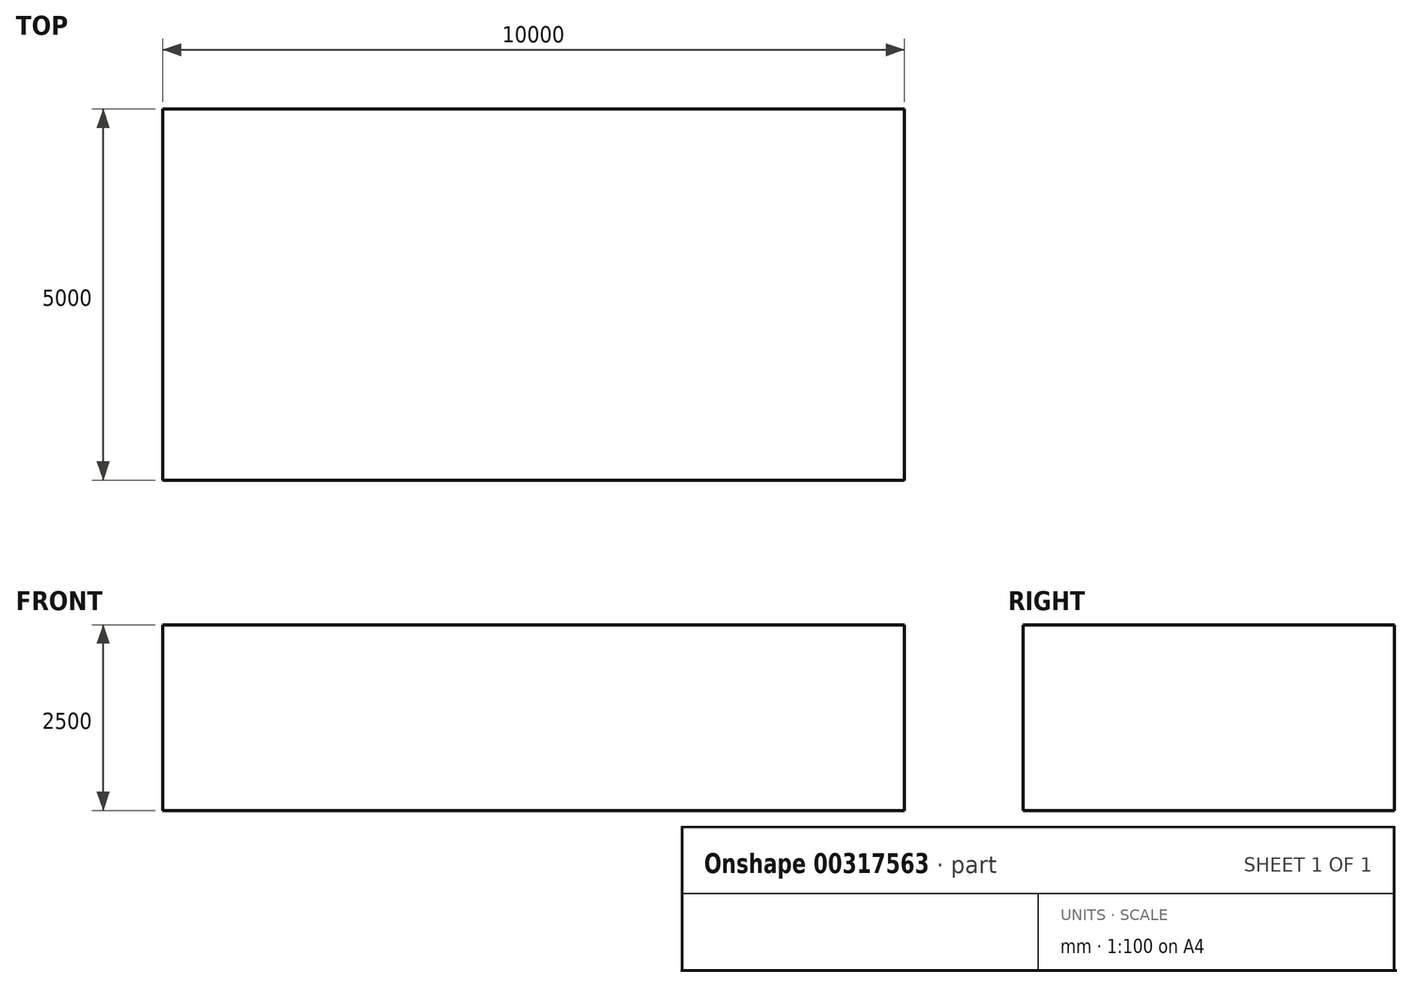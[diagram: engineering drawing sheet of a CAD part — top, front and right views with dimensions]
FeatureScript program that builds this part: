
annotation { "Feature Type Name" : "Feature", "Feature Type Description" : "" }
export const myFeature = defineFeature(function(context is Context, id is Id, definition is map)
    precondition{}
    {
        {
            var Q0;
            Q0=qCreatedBy(makeId("Right.planeOp"),FACE);
            var sketch = newSketch(context, id + "F0", { "sketchPlane" : qUnion([Q0])});
            skLineSegment(sketch, "E0.bottom", {"start": v(0, 0) * mm, "end": v(-5000, 0) * mm});
            skLineSegment(sketch, "E0.top", {"start": v(0, -2500) * mm, "end": v(-5000, -2500) * mm});
            skLineSegment(sketch, "E0.left", {"start": v(0, 0) * mm, "end": v(0, -2500) * mm});
            skLineSegment(sketch, "E0.right", {"start": v(-5000, 0) * mm, "end": v(-5000, -2500) * mm});
            skSolve(sketch);
        }
        {
            var Q0;
            Q0 = qSketchRegion(id + "F0", true);
            extrude(context, id + "F1", {"entities" : qUnion([Q0]), "depth" : 10000 * mm});
        }
    });
